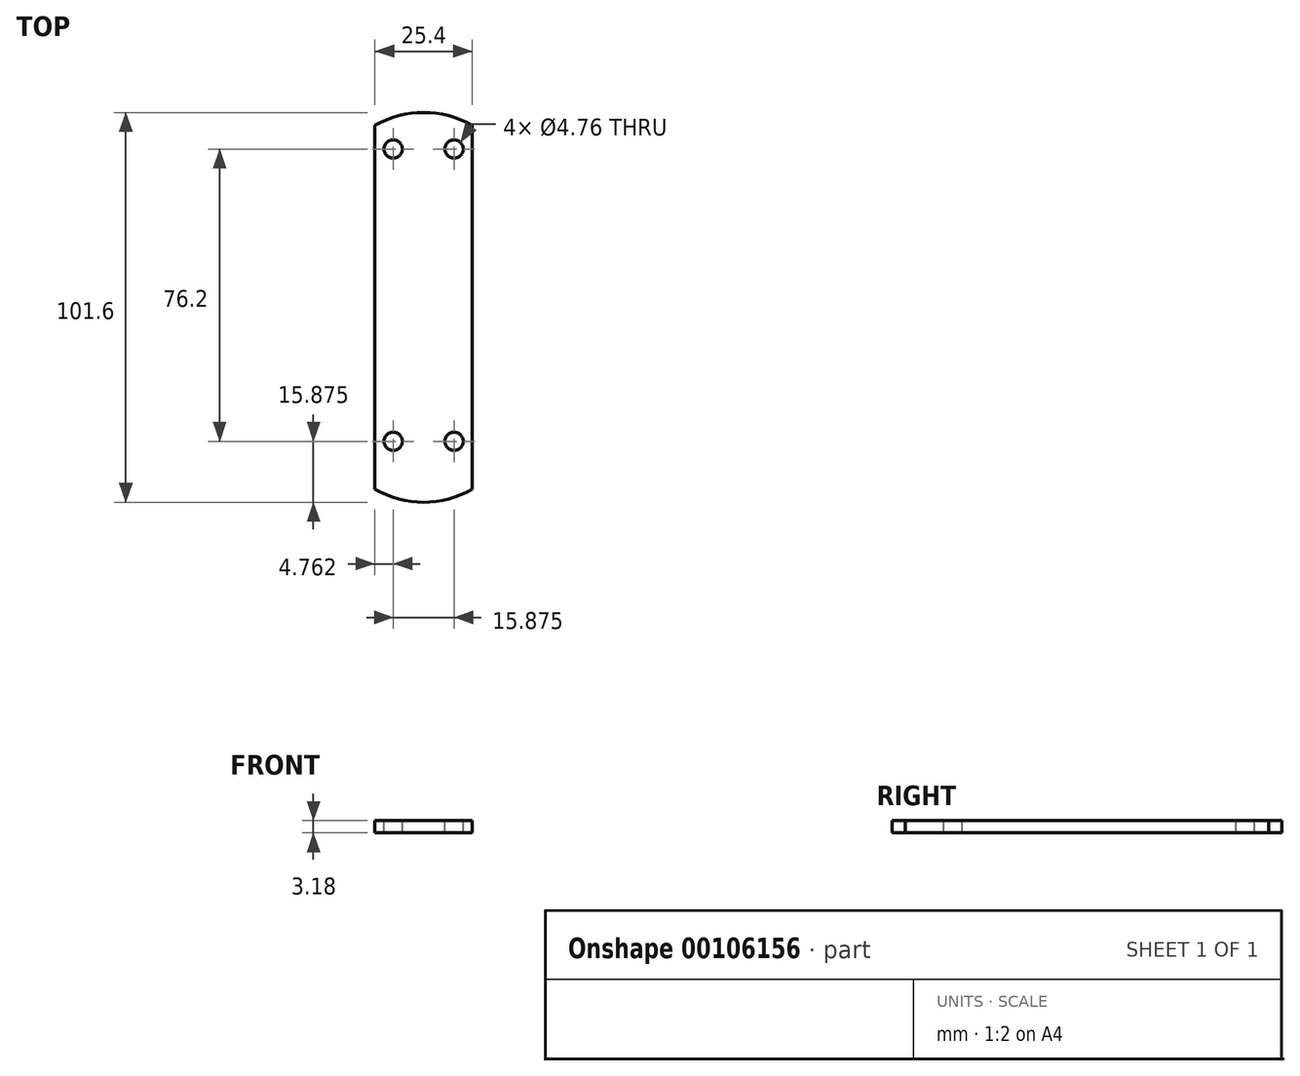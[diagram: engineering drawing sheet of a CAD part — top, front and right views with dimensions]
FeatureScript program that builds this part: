
annotation { "Feature Type Name" : "Feature", "Feature Type Description" : "" }
export const myFeature = defineFeature(function(context is Context, id is Id, definition is map)
    precondition{}
    {
        {
            var Q0;
            Q0=qCreatedBy(makeId("Top.planeOp"),FACE);
            var sketch = newSketch(context, id + "F0", { "sketchPlane" : qUnion([Q0])});
            skLineSegment(sketch, "E0.left", {"start": v(12.7, 47.4) * mm, "end": v(12.7, -47.4) * mm});
            skLineSegment(sketch, "E0.right", {"start": v(-12.7, 47.4) * mm, "end": v(-12.7, -47.4) * mm});
            skPoint(sketch, "E0.middle", {"position": v(0, 0) * mm});
            skLineSegment(sketch, "E1", {"start": v(0, -25.4) * mm, "end": v(0, 25.4) * mm});
            skArc(sketch, "E2", {"start": v(-12.7, -47.4) * mm, "mid": v(0, -50.8) * mm, "end": v(12.7, -47.4) * mm});
            skArc(sketch, "E3.trimOffspring", {"start": v(12.7, 47.4) * mm, "mid": v(0, 50.8) * mm, "end": v(-12.7, 47.4) * mm});
            skPoint(sketch, "E4", {"position": v(0, 50.8) * mm});
            skPoint(sketch, "E5", {"position": v(0, -50.8) * mm});
            skLineSegment(sketch, "E6", {"start": v(-12.7, 0) * mm, "end": v(12.7, 0) * mm});
            skSolve(sketch);
        }
        {
            var Q0;
            Q0 = qSketchRegion(id + "F0", true);
            extrude(context, id + "F1", {"entities" : qUnion([Q0]), "depth" : 3.17 * mm});
        }
        {
            var Q0;
            Q0=makeQuery(id+"F1.opExtrude","CAP_FACE",FACE,{"disambiguationData":[OSD([sQuery(id+"F0.wireOp",EDGE,"E0.left"),sQuery(id+"F0.wireOp",EDGE,"E0.right"),sQuery(id+"F0.wireOp",EDGE,"E2"),sQuery(id+"F0.wireOp",EDGE,"E3.trimOffspring")])],"isStart":false});
            var sketch = newSketch(context, id + "F2", { "sketchPlane" : qUnion([Q0])});
            skLineSegment(sketch, "E7.bottom", {"start": v(7.94, 41.27) * mm, "end": v(-7.94, 41.27) * mm, "construction": true});
            skLineSegment(sketch, "E7.top", {"start": v(7.94, -34.92) * mm, "end": v(-7.94, -34.92) * mm, "construction": true});
            skLineSegment(sketch, "E7.left", {"start": v(7.94, 41.27) * mm, "end": v(7.94, -34.92) * mm, "construction": true});
            skLineSegment(sketch, "E7.right", {"start": v(-7.94, 41.27) * mm, "end": v(-7.94, -34.92) * mm, "construction": true});
            skPoint(sketch, "E7.middle", {"position": v(0, 3.18) * mm});
            skCircle(sketch, "E8", {"center": v(-7.94, 41.27) * mm, "radius": 2.38 * mm});
            skCircle(sketch, "E9", {"center": v(7.94, 41.27) * mm, "radius": 2.38 * mm});
            skCircle(sketch, "E10", {"center": v(-7.94, -34.92) * mm, "radius": 2.38 * mm});
            skCircle(sketch, "E11", {"center": v(7.94, -34.92) * mm, "radius": 2.38 * mm});
            skLineSegment(sketch, "E12", {"start": v(0, 0) * mm, "end": v(0, 3.18) * mm});
            skSolve(sketch);
        }
        {
            var Q0;
            Q0 = qSketchRegion(id + "F2", true);
            extrude(context, id + "F3", {"entities" : qUnion([Q0]), "operationType" : NewBodyOperationType.REMOVE, "endBound" : BoundingType.UP_TO_NEXT, "oppositeDirection" : true, "depth" : 25.4 * mm});
        }
    });
